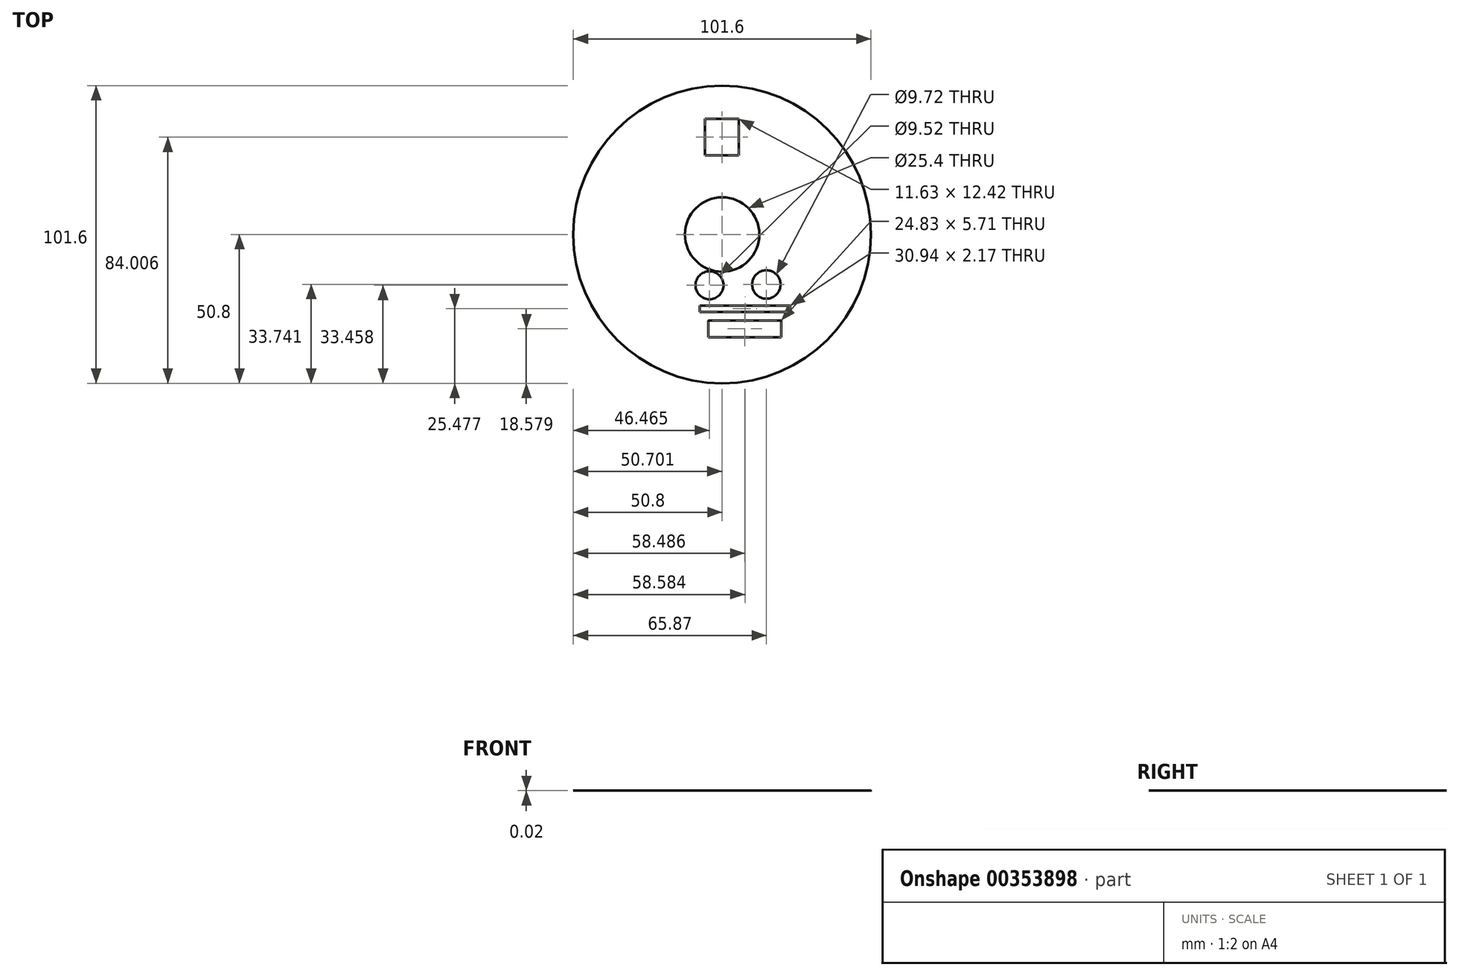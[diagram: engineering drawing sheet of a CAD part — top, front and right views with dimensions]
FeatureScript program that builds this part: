
annotation { "Feature Type Name" : "Feature", "Feature Type Description" : "" }
export const myFeature = defineFeature(function(context is Context, id is Id, definition is map)
    precondition{}
    {
        {
            var Q0;
            Q0=qCreatedBy(makeId("Top.planeOp"),FACE);
            var sketch = newSketch(context, id + "F0", { "sketchPlane" : qUnion([Q0])});
            skCircle(sketch, "E0", {"center": v(0, 0) * mm, "radius": 12.7 * mm});
            skCircle(sketch, "E1", {"center": v(0, 0) * mm, "radius": 50.8 * mm});
            skLineSegment(sketch, "E2.bottom", {"start": v(-5.91, 39.41) * mm, "end": v(5.71, 39.41) * mm});
            skLineSegment(sketch, "E2.top", {"start": v(-5.91, 27) * mm, "end": v(5.71, 27) * mm});
            skLineSegment(sketch, "E2.left", {"start": v(-5.91, 39.41) * mm, "end": v(-5.91, 27) * mm});
            skLineSegment(sketch, "E2.right", {"start": v(5.71, 39.41) * mm, "end": v(5.71, 27) * mm});
            skLineSegment(sketch, "E3.bottom", {"start": v(-4.73, -29.36) * mm, "end": v(20.1, -29.36) * mm});
            skLineSegment(sketch, "E3.top", {"start": v(-4.73, -35.08) * mm, "end": v(20.1, -35.08) * mm});
            skLineSegment(sketch, "E3.left", {"start": v(-4.73, -29.36) * mm, "end": v(-4.73, -35.08) * mm});
            skLineSegment(sketch, "E3.right", {"start": v(20.1, -29.36) * mm, "end": v(20.1, -35.08) * mm});
            skCircle(sketch, "E4", {"center": v(15.07, -17.06) * mm, "radius": 4.86 * mm});
            skCircle(sketch, "E5", {"center": v(-4.34, -17.34) * mm, "radius": 4.76 * mm});
            skLineSegment(sketch, "E6.bottom", {"start": v(-7.69, -24.24) * mm, "end": v(23.25, -24.24) * mm});
            skLineSegment(sketch, "E6.top", {"start": v(-7.69, -26.4) * mm, "end": v(23.25, -26.4) * mm});
            skLineSegment(sketch, "E6.left", {"start": v(-7.69, -24.24) * mm, "end": v(-7.69, -26.4) * mm});
            skLineSegment(sketch, "E6.right", {"start": v(23.25, -24.24) * mm, "end": v(23.25, -26.4) * mm});
            skSolve(sketch);
        }
        {
            var Q0;
            Q0=makeQuery(id+"F0.imprint","IMPRINT",FACE,{"disambiguationData":[TD([[makeQuery(id+"F0.imprint","IMPRINT",EDGE,{"derivedFrom":sQuery(id+"F0.wireOp",EDGE,"E0")}),-1.0]])]});
            extrude(context, id + "F1", {"entities" : qUnion([Q0]), "endBound" : BoundingType.SYMMETRIC, "depth" : 1 / 50.8 * mm});
        }
    });
